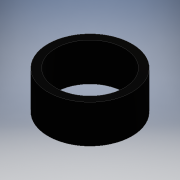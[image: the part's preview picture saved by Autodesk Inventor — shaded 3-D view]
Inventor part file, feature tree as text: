
AUTODESK INVENTOR PART (.ipt)
format: ipt  version: 2016 (Build 200138000, 138)  size: 92,672 bytes
history: native  units: mm
features: other x1, extrude x1, sketch x1
ambient origin geometry x8: Origin, YZ Plane, XZ Plane, XY Plane, X Axis, Y Axis, Z Axis, Center Point
bodies: Body1 (feature_tree)
feature tree (3):
  other  "ソリッド1"
  extrude  "押し出し1"  Depth=9.0mm
  sketch  "スケッチ1"
